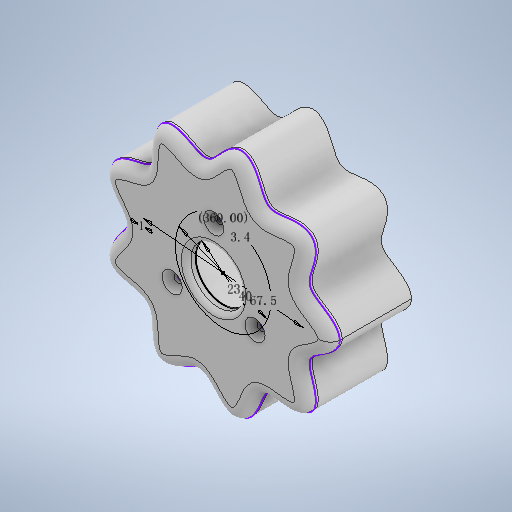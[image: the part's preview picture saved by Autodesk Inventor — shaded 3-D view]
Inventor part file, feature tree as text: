
AUTODESK INVENTOR PART (.ipt)
format: ipt  version: 2025 (Build 290162000, 162)  size: 517,632 bytes
history: native  units: mm
features: sketch x2, extrude x2, chamfer x1, fillet x1, other x1
ambient origin geometry x8: Origin, YZ Plane, XZ Plane, XY Plane, X Axis, Y Axis, Z Axis, Center Point
bodies: 实体1 (feature_tree)
feature tree (7):
  sketch  "草图1"  dims[d0=67.5mm d1=40.0mm]
  extrude  "拉伸1"  Depth=40.0mm
  extrude  "拉伸2"  Depth=30.0mm TaperAngle=360.0deg
  chamfer  "倒角1"  Distance=1.0mm
  fillet  "圆角1"  Radius=3600.0mm
  sketch  "草图 - 环形阵列1"  dims[d2=3.4mm d3=30.0mm d5=360.0deg d7=1.0mm d8=0.0mm d9=3600.0mm d10=23.0mm d11=4.0mm d12=0.0mm d13=30.0mm d14=0.0mm d15=2.5mm d16=2.0mm d17=45.0deg d18=2.0mm d19=5.0mm]
  other  "二维表达式曲线1"
